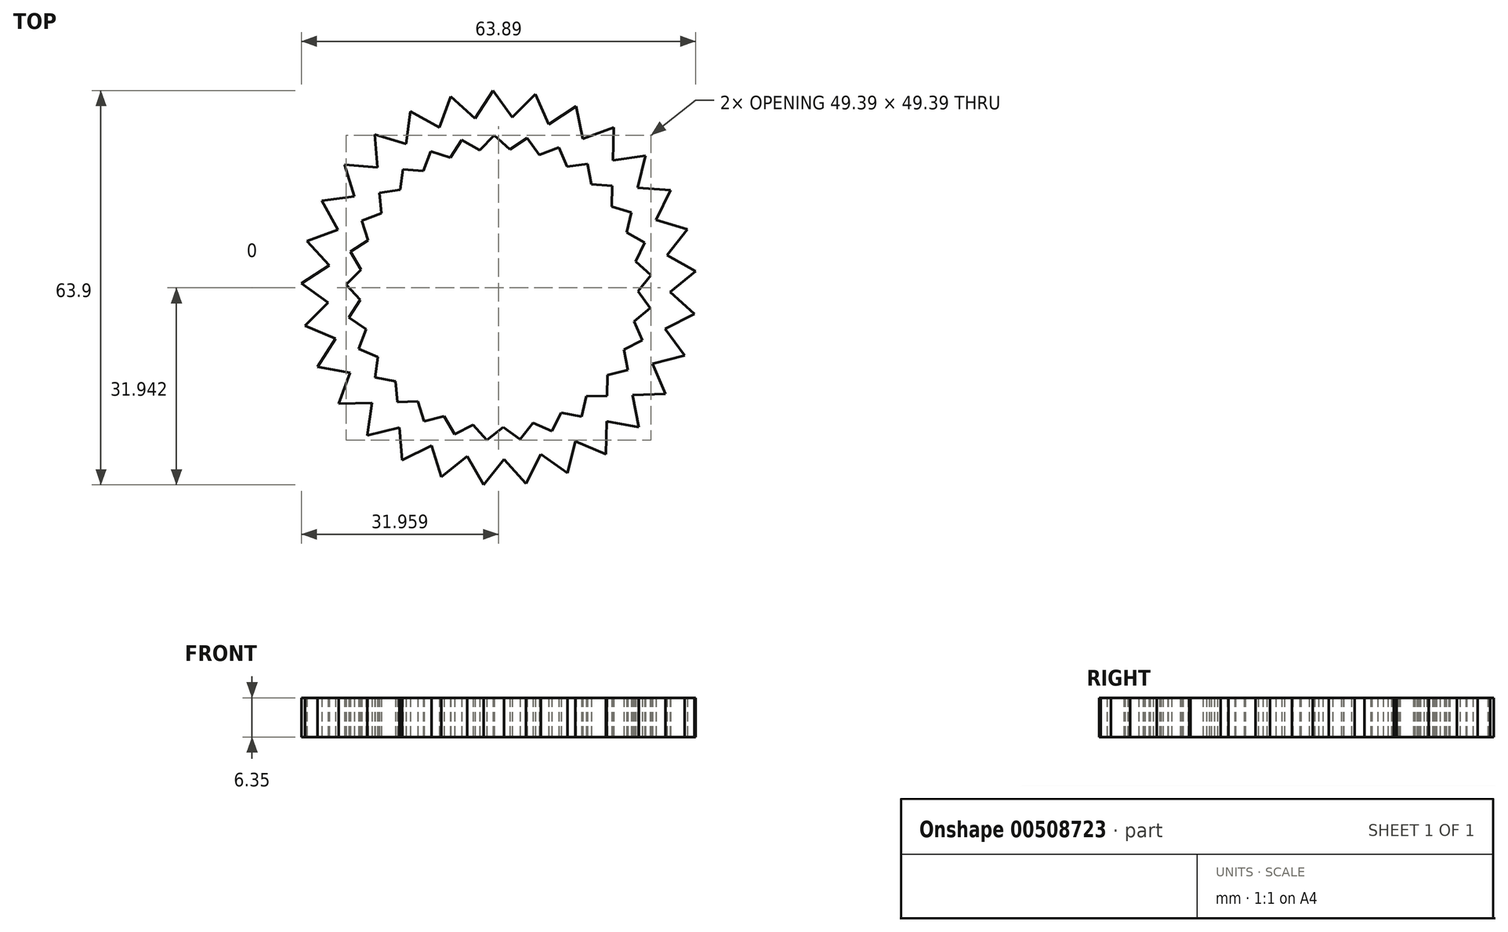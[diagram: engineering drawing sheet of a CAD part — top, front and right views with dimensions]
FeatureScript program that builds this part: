
annotation { "Feature Type Name" : "Feature", "Feature Type Description" : "" }
export const myFeature = defineFeature(function(context is Context, id is Id, definition is map)
    precondition{}
    {
        {
            var Q0;
            Q0=qCreatedBy(makeId("Top.planeOp"),FACE);
            var sketch = newSketch(context, id + "F0", { "sketchPlane" : qUnion([Q0])});
            skLineSegment(sketch, "E0", {"start": v(-25.94, -18.75) * mm, "end": v(-7.82, 31.04) * mm});
            skLineSegment(sketch, "E1", {"start": v(-7.82, 31.04) * mm, "end": v(31.73, -4.22) * mm});
            skLineSegment(sketch, "E2", {"start": v(31.73, -4.22) * mm, "end": v(-15.66, -27.91) * mm});
            skLineSegment(sketch, "E3", {"start": v(-15.66, -27.91) * mm, "end": v(-20.13, 24.88) * mm});
            skLineSegment(sketch, "E4", {"start": v(-20.13, 24.88) * mm, "end": v(30.57, 9.5) * mm});
            skLineSegment(sketch, "E5", {"start": v(30.57, 9.5) * mm, "end": v(-2.5, -31.9) * mm});
            skLineSegment(sketch, "E6", {"start": v(-2.5, -31.9) * mm, "end": v(-28.72, 14.13) * mm});
            skLineSegment(sketch, "E7", {"start": v(-28.72, 14.13) * mm, "end": v(23.76, 21.45) * mm});
            skLineSegment(sketch, "E8", {"start": v(23.76, 21.45) * mm, "end": v(11.13, -30) * mm});
            skLineSegment(sketch, "E9", {"start": v(11.13, -30) * mm, "end": v(-32, 0.77) * mm});
            skLineSegment(sketch, "E10", {"start": v(-32, 0.77) * mm, "end": v(12.55, 29.44) * mm});
            skLineSegment(sketch, "E11", {"start": v(12.55, 29.44) * mm, "end": v(22.7, -22.56) * mm});
            skLineSegment(sketch, "E12", {"start": v(22.7, -22.56) * mm, "end": v(-29.36, -12.74) * mm});
            skLineSegment(sketch, "E13", {"start": v(-29.36, -12.74) * mm, "end": v(-0.97, 32) * mm});
            skLineSegment(sketch, "E14", {"start": v(-0.97, 32) * mm, "end": v(30.08, -10.94) * mm});
            skLineSegment(sketch, "E15", {"start": v(30.08, -10.94) * mm, "end": v(-21.3, -23.9) * mm});
            skLineSegment(sketch, "E16", {"start": v(-21.3, -23.9) * mm, "end": v(-14.31, 28.63) * mm});
            skLineSegment(sketch, "E17", {"start": v(-14.31, 28.63) * mm, "end": v(31.9, 2.7) * mm});
            skLineSegment(sketch, "E18", {"start": v(31.9, 2.7) * mm, "end": v(-9.3, -30.63) * mm});
            skLineSegment(sketch, "E19", {"start": v(-9.3, -30.63) * mm, "end": v(-25, 19.97) * mm});
            skLineSegment(sketch, "E20", {"start": v(-25, 19.97) * mm, "end": v(27.81, 15.84) * mm});
            skLineSegment(sketch, "E21", {"start": v(27.81, 15.84) * mm, "end": v(4.42, -31.7) * mm});
            skLineSegment(sketch, "E22", {"start": v(4.42, -31.7) * mm, "end": v(-31.08, 7.63) * mm});
            skLineSegment(sketch, "E23", {"start": v(-31.08, 7.63) * mm, "end": v(18.6, 26.05) * mm});
            skLineSegment(sketch, "E24", {"start": v(18.6, 26.05) * mm, "end": v(17.32, -26.91) * mm});
            skLineSegment(sketch, "E25", {"start": v(17.32, -26.91) * mm, "end": v(-31.41, -6.13) * mm});
            skLineSegment(sketch, "E26", {"start": v(-31.41, -6.13) * mm, "end": v(5.93, 31.45) * mm});
            skLineSegment(sketch, "E27", {"start": v(5.93, 31.45) * mm, "end": v(27.02, -17.15) * mm});
            skLineSegment(sketch, "E28", {"start": v(27.02, -17.15) * mm, "end": v(-25.94, -18.75) * mm});
            skSolve(sketch);
        }
        {
            var Q0;
            {var subQ0=sQuery(id+"F0.wireOp",EDGE,"E28");var subQ1=sQuery(id+"F0.wireOp",EDGE,"E0");var subQ2=makeQuery(id+"F0.imprint","INTERSECT",VERTEX,{"derivedFrom":[subQ1,subQ0]});Q0=makeQuery(id+"F0.imprint","IMPRINT",FACE,{"disambiguationData":[TD([[makeQuery(id+"F0.imprint","IMPRINT",EDGE,{"disambiguationData":[TD([[subQ2,-1.0]])],"derivedFrom":subQ1}),-1.0]])]});}
            var Q1;
            {var subQ0=sQuery(id+"F0.wireOp",EDGE,"E15");var subQ1=sQuery(id+"F0.wireOp",EDGE,"E3");var subQ2=makeQuery(id+"F0.imprint","INTERSECT",VERTEX,{"derivedFrom":[subQ1,subQ0]});Q1=makeQuery(id+"F0.imprint","IMPRINT",FACE,{"disambiguationData":[TD([[makeQuery(id+"F0.imprint","IMPRINT",EDGE,{"disambiguationData":[TD([[subQ2,-1.0]])],"derivedFrom":subQ1}),1.0]])]});}
            var Q2;
            {var subQ0=sQuery(id+"F0.wireOp",EDGE,"E3");var subQ1=sQuery(id+"F0.wireOp",EDGE,"E2");var subQ2=makeQuery(id+"F0.imprint","INTERSECT",VERTEX,{"derivedFrom":[subQ1,subQ0]});Q2=makeQuery(id+"F0.imprint","IMPRINT",FACE,{"disambiguationData":[TD([[makeQuery(id+"F0.imprint","IMPRINT",EDGE,{"disambiguationData":[TD([[subQ2,1.0]])],"derivedFrom":subQ1}),-1.0]])]});}
            var Q3;
            {var subQ0=sQuery(id+"F0.wireOp",EDGE,"E19");var subQ1=sQuery(id+"F0.wireOp",EDGE,"E2");var subQ2=makeQuery(id+"F0.imprint","INTERSECT",VERTEX,{"derivedFrom":[subQ1,subQ0]});Q3=makeQuery(id+"F0.imprint","IMPRINT",FACE,{"disambiguationData":[TD([[makeQuery(id+"F0.imprint","IMPRINT",EDGE,{"disambiguationData":[TD([[subQ2,1.0]])],"derivedFrom":subQ1}),1.0]])]});}
            var Q4;
            {var subQ0=sQuery(id+"F0.wireOp",EDGE,"E6");var subQ1=sQuery(id+"F0.wireOp",EDGE,"E5");var subQ2=makeQuery(id+"F0.imprint","INTERSECT",VERTEX,{"derivedFrom":[subQ1,subQ0]});Q4=makeQuery(id+"F0.imprint","IMPRINT",FACE,{"disambiguationData":[TD([[makeQuery(id+"F0.imprint","IMPRINT",EDGE,{"disambiguationData":[TD([[subQ2,1.0]])],"derivedFrom":subQ1}),-1.0]])]});}
            var Q5;
            {var subQ0=sQuery(id+"F0.wireOp",EDGE,"E9");var subQ1=sQuery(id+"F0.wireOp",EDGE,"E8");var subQ2=makeQuery(id+"F0.imprint","INTERSECT",VERTEX,{"derivedFrom":[subQ1,subQ0]});Q5=makeQuery(id+"F0.imprint","IMPRINT",FACE,{"disambiguationData":[TD([[makeQuery(id+"F0.imprint","IMPRINT",EDGE,{"disambiguationData":[TD([[subQ2,1.0]])],"derivedFrom":subQ1}),-1.0]])]});}
            var Q6;
            {var subQ0=sQuery(id+"F0.wireOp",EDGE,"E25");var subQ1=sQuery(id+"F0.wireOp",EDGE,"E8");var subQ2=makeQuery(id+"F0.imprint","INTERSECT",VERTEX,{"derivedFrom":[subQ1,subQ0]});Q6=makeQuery(id+"F0.imprint","IMPRINT",FACE,{"disambiguationData":[TD([[makeQuery(id+"F0.imprint","IMPRINT",EDGE,{"disambiguationData":[TD([[subQ2,1.0]])],"derivedFrom":subQ1}),1.0]])]});}
            var Q7;
            {var subQ0=sQuery(id+"F0.wireOp",EDGE,"E12");var subQ1=sQuery(id+"F0.wireOp",EDGE,"E11");var subQ2=makeQuery(id+"F0.imprint","INTERSECT",VERTEX,{"derivedFrom":[subQ1,subQ0]});Q7=makeQuery(id+"F0.imprint","IMPRINT",FACE,{"disambiguationData":[TD([[makeQuery(id+"F0.imprint","IMPRINT",EDGE,{"disambiguationData":[TD([[subQ2,1.0]])],"derivedFrom":subQ1}),-1.0]])]});}
            var Q8;
            {var subQ0=sQuery(id+"F0.wireOp",EDGE,"E28");var subQ1=sQuery(id+"F0.wireOp",EDGE,"E11");var subQ2=makeQuery(id+"F0.imprint","INTERSECT",VERTEX,{"derivedFrom":[subQ1,subQ0]});Q8=makeQuery(id+"F0.imprint","IMPRINT",FACE,{"disambiguationData":[TD([[makeQuery(id+"F0.imprint","IMPRINT",EDGE,{"disambiguationData":[TD([[subQ2,1.0]])],"derivedFrom":subQ1}),1.0]])]});}
            var Q9;
            {var subQ0=sQuery(id+"F0.wireOp",EDGE,"E14");var subQ1=sQuery(id+"F0.wireOp",EDGE,"E2");var subQ2=makeQuery(id+"F0.imprint","INTERSECT",VERTEX,{"derivedFrom":[subQ1,subQ0]});Q9=makeQuery(id+"F0.imprint","IMPRINT",FACE,{"disambiguationData":[TD([[makeQuery(id+"F0.imprint","IMPRINT",EDGE,{"disambiguationData":[TD([[subQ2,-1.0]])],"derivedFrom":subQ1}),1.0]])]});}
            var Q10;
            {var subQ0=sQuery(id+"F0.wireOp",EDGE,"E2");var subQ1=sQuery(id+"F0.wireOp",EDGE,"E1");var subQ2=makeQuery(id+"F0.imprint","INTERSECT",VERTEX,{"derivedFrom":[subQ1,subQ0]});Q10=makeQuery(id+"F0.imprint","IMPRINT",FACE,{"disambiguationData":[TD([[makeQuery(id+"F0.imprint","IMPRINT",EDGE,{"disambiguationData":[TD([[subQ2,1.0]])],"derivedFrom":subQ1}),-1.0]])]});}
            var Q11;
            {var subQ0=sQuery(id+"F0.wireOp",EDGE,"E18");var subQ1=sQuery(id+"F0.wireOp",EDGE,"E1");var subQ2=makeQuery(id+"F0.imprint","INTERSECT",VERTEX,{"derivedFrom":[subQ1,subQ0]});Q11=makeQuery(id+"F0.imprint","IMPRINT",FACE,{"disambiguationData":[TD([[makeQuery(id+"F0.imprint","IMPRINT",EDGE,{"disambiguationData":[TD([[subQ2,1.0]])],"derivedFrom":subQ1}),1.0]])]});}
            var Q12;
            {var subQ0=sQuery(id+"F0.wireOp",EDGE,"E5");var subQ1=sQuery(id+"F0.wireOp",EDGE,"E4");var subQ2=makeQuery(id+"F0.imprint","INTERSECT",VERTEX,{"derivedFrom":[subQ1,subQ0]});Q12=makeQuery(id+"F0.imprint","IMPRINT",FACE,{"disambiguationData":[TD([[makeQuery(id+"F0.imprint","IMPRINT",EDGE,{"disambiguationData":[TD([[subQ2,1.0]])],"derivedFrom":subQ1}),-1.0]])]});}
            var Q13;
            {var subQ0=sQuery(id+"F0.wireOp",EDGE,"E21");var subQ1=sQuery(id+"F0.wireOp",EDGE,"E4");var subQ2=makeQuery(id+"F0.imprint","INTERSECT",VERTEX,{"derivedFrom":[subQ1,subQ0]});Q13=makeQuery(id+"F0.imprint","IMPRINT",FACE,{"disambiguationData":[TD([[makeQuery(id+"F0.imprint","IMPRINT",EDGE,{"disambiguationData":[TD([[subQ2,1.0]])],"derivedFrom":subQ1}),1.0]])]});}
            var Q14;
            {var subQ0=sQuery(id+"F0.wireOp",EDGE,"E8");var subQ1=sQuery(id+"F0.wireOp",EDGE,"E7");var subQ2=makeQuery(id+"F0.imprint","INTERSECT",VERTEX,{"derivedFrom":[subQ1,subQ0]});Q14=makeQuery(id+"F0.imprint","IMPRINT",FACE,{"disambiguationData":[TD([[makeQuery(id+"F0.imprint","IMPRINT",EDGE,{"disambiguationData":[TD([[subQ2,1.0]])],"derivedFrom":subQ1}),-1.0]])]});}
            var Q15;
            {var subQ0=sQuery(id+"F0.wireOp",EDGE,"E24");var subQ1=sQuery(id+"F0.wireOp",EDGE,"E7");var subQ2=makeQuery(id+"F0.imprint","INTERSECT",VERTEX,{"derivedFrom":[subQ1,subQ0]});Q15=makeQuery(id+"F0.imprint","IMPRINT",FACE,{"disambiguationData":[TD([[makeQuery(id+"F0.imprint","IMPRINT",EDGE,{"disambiguationData":[TD([[subQ2,1.0]])],"derivedFrom":subQ1}),1.0]])]});}
            var Q16;
            {var subQ0=sQuery(id+"F0.wireOp",EDGE,"E11");var subQ1=sQuery(id+"F0.wireOp",EDGE,"E10");var subQ2=makeQuery(id+"F0.imprint","INTERSECT",VERTEX,{"derivedFrom":[subQ1,subQ0]});Q16=makeQuery(id+"F0.imprint","IMPRINT",FACE,{"disambiguationData":[TD([[makeQuery(id+"F0.imprint","IMPRINT",EDGE,{"disambiguationData":[TD([[subQ2,1.0]])],"derivedFrom":subQ1}),-1.0]])]});}
            var Q17;
            {var subQ0=sQuery(id+"F0.wireOp",EDGE,"E27");var subQ1=sQuery(id+"F0.wireOp",EDGE,"E10");var subQ2=makeQuery(id+"F0.imprint","INTERSECT",VERTEX,{"derivedFrom":[subQ1,subQ0]});Q17=makeQuery(id+"F0.imprint","IMPRINT",FACE,{"disambiguationData":[TD([[makeQuery(id+"F0.imprint","IMPRINT",EDGE,{"disambiguationData":[TD([[subQ2,1.0]])],"derivedFrom":subQ1}),1.0]])]});}
            var Q18;
            {var subQ0=sQuery(id+"F0.wireOp",EDGE,"E13");var subQ1=sQuery(id+"F0.wireOp",EDGE,"E1");var subQ2=makeQuery(id+"F0.imprint","INTERSECT",VERTEX,{"derivedFrom":[subQ1,subQ0]});Q18=makeQuery(id+"F0.imprint","IMPRINT",FACE,{"disambiguationData":[TD([[makeQuery(id+"F0.imprint","IMPRINT",EDGE,{"disambiguationData":[TD([[subQ2,-1.0]])],"derivedFrom":subQ1}),1.0]])]});}
            var Q19;
            {var subQ0=sQuery(id+"F0.wireOp",EDGE,"E1");var subQ1=sQuery(id+"F0.wireOp",EDGE,"E0");var subQ2=makeQuery(id+"F0.imprint","INTERSECT",VERTEX,{"derivedFrom":[subQ1,subQ0]});Q19=makeQuery(id+"F0.imprint","IMPRINT",FACE,{"disambiguationData":[TD([[makeQuery(id+"F0.imprint","IMPRINT",EDGE,{"disambiguationData":[TD([[subQ2,1.0]])],"derivedFrom":subQ1}),-1.0]])]});}
            var Q20;
            {var subQ0=sQuery(id+"F0.wireOp",EDGE,"E17");var subQ1=sQuery(id+"F0.wireOp",EDGE,"E0");var subQ2=makeQuery(id+"F0.imprint","INTERSECT",VERTEX,{"derivedFrom":[subQ1,subQ0]});Q20=makeQuery(id+"F0.imprint","IMPRINT",FACE,{"disambiguationData":[TD([[makeQuery(id+"F0.imprint","IMPRINT",EDGE,{"disambiguationData":[TD([[subQ2,1.0]])],"derivedFrom":subQ1}),1.0]])]});}
            var Q21;
            {var subQ0=sQuery(id+"F0.wireOp",EDGE,"E4");var subQ1=sQuery(id+"F0.wireOp",EDGE,"E3");var subQ2=makeQuery(id+"F0.imprint","INTERSECT",VERTEX,{"derivedFrom":[subQ1,subQ0]});Q21=makeQuery(id+"F0.imprint","IMPRINT",FACE,{"disambiguationData":[TD([[makeQuery(id+"F0.imprint","IMPRINT",EDGE,{"disambiguationData":[TD([[subQ2,1.0]])],"derivedFrom":subQ1}),-1.0]])]});}
            var Q22;
            {var subQ0=sQuery(id+"F0.wireOp",EDGE,"E20");var subQ1=sQuery(id+"F0.wireOp",EDGE,"E3");var subQ2=makeQuery(id+"F0.imprint","INTERSECT",VERTEX,{"derivedFrom":[subQ1,subQ0]});Q22=makeQuery(id+"F0.imprint","IMPRINT",FACE,{"disambiguationData":[TD([[makeQuery(id+"F0.imprint","IMPRINT",EDGE,{"disambiguationData":[TD([[subQ2,1.0]])],"derivedFrom":subQ1}),1.0]])]});}
            var Q23;
            {var subQ0=sQuery(id+"F0.wireOp",EDGE,"E7");var subQ1=sQuery(id+"F0.wireOp",EDGE,"E6");var subQ2=makeQuery(id+"F0.imprint","INTERSECT",VERTEX,{"derivedFrom":[subQ1,subQ0]});Q23=makeQuery(id+"F0.imprint","IMPRINT",FACE,{"disambiguationData":[TD([[makeQuery(id+"F0.imprint","IMPRINT",EDGE,{"disambiguationData":[TD([[subQ2,1.0]])],"derivedFrom":subQ1}),-1.0]])]});}
            var Q24;
            {var subQ0=sQuery(id+"F0.wireOp",EDGE,"E23");var subQ1=sQuery(id+"F0.wireOp",EDGE,"E6");var subQ2=makeQuery(id+"F0.imprint","INTERSECT",VERTEX,{"derivedFrom":[subQ1,subQ0]});Q24=makeQuery(id+"F0.imprint","IMPRINT",FACE,{"disambiguationData":[TD([[makeQuery(id+"F0.imprint","IMPRINT",EDGE,{"disambiguationData":[TD([[subQ2,1.0]])],"derivedFrom":subQ1}),1.0]])]});}
            var Q25;
            {var subQ0=sQuery(id+"F0.wireOp",EDGE,"E10");var subQ1=sQuery(id+"F0.wireOp",EDGE,"E9");var subQ2=makeQuery(id+"F0.imprint","INTERSECT",VERTEX,{"derivedFrom":[subQ1,subQ0]});Q25=makeQuery(id+"F0.imprint","IMPRINT",FACE,{"disambiguationData":[TD([[makeQuery(id+"F0.imprint","IMPRINT",EDGE,{"disambiguationData":[TD([[subQ2,1.0]])],"derivedFrom":subQ1}),-1.0]])]});}
            var Q26;
            {var subQ0=sQuery(id+"F0.wireOp",EDGE,"E26");var subQ1=sQuery(id+"F0.wireOp",EDGE,"E9");var subQ2=makeQuery(id+"F0.imprint","INTERSECT",VERTEX,{"derivedFrom":[subQ1,subQ0]});Q26=makeQuery(id+"F0.imprint","IMPRINT",FACE,{"disambiguationData":[TD([[makeQuery(id+"F0.imprint","IMPRINT",EDGE,{"disambiguationData":[TD([[subQ2,1.0]])],"derivedFrom":subQ1}),1.0]])]});}
            var Q27;
            {var subQ0=sQuery(id+"F0.wireOp",EDGE,"E12");var subQ1=sQuery(id+"F0.wireOp",EDGE,"E0");var subQ2=makeQuery(id+"F0.imprint","INTERSECT",VERTEX,{"derivedFrom":[subQ1,subQ0]});Q27=makeQuery(id+"F0.imprint","IMPRINT",FACE,{"disambiguationData":[TD([[makeQuery(id+"F0.imprint","IMPRINT",EDGE,{"disambiguationData":[TD([[subQ2,-1.0]])],"derivedFrom":subQ1}),1.0]])]});}
            var Q28;
            {var subQ0=sQuery(id+"F0.wireOp",EDGE,"E22");var subQ1=sQuery(id+"F0.wireOp",EDGE,"E5");var subQ2=makeQuery(id+"F0.imprint","INTERSECT",VERTEX,{"derivedFrom":[subQ1,subQ0]});Q28=makeQuery(id+"F0.imprint","IMPRINT",FACE,{"disambiguationData":[TD([[makeQuery(id+"F0.imprint","IMPRINT",EDGE,{"disambiguationData":[TD([[subQ2,1.0]])],"derivedFrom":subQ1}),1.0]])]});}
            var Q29;
            {var subQ0=sQuery(id+"F0.wireOp",EDGE,"E19");var subQ1=sQuery(id+"F0.wireOp",EDGE,"E2");var subQ2=makeQuery(id+"F0.imprint","INTERSECT",VERTEX,{"derivedFrom":[subQ1,subQ0]});Q29=makeQuery(id+"F0.imprint","IMPRINT",FACE,{"disambiguationData":[TD([[makeQuery(id+"F0.imprint","IMPRINT",EDGE,{"disambiguationData":[TD([[subQ2,1.0]])],"derivedFrom":subQ1}),-1.0]])]});}
            var Q30;
            {var subQ0=sQuery(id+"F0.wireOp",EDGE,"E22");var subQ1=sQuery(id+"F0.wireOp",EDGE,"E5");var subQ2=makeQuery(id+"F0.imprint","INTERSECT",VERTEX,{"derivedFrom":[subQ1,subQ0]});Q30=makeQuery(id+"F0.imprint","IMPRINT",FACE,{"disambiguationData":[TD([[makeQuery(id+"F0.imprint","IMPRINT",EDGE,{"disambiguationData":[TD([[subQ2,1.0]])],"derivedFrom":subQ1}),-1.0]])]});}
            var Q31;
            {var subQ0=sQuery(id+"F0.wireOp",EDGE,"E22");var subQ1=sQuery(id+"F0.wireOp",EDGE,"E2");var subQ2=makeQuery(id+"F0.imprint","INTERSECT",VERTEX,{"derivedFrom":[subQ1,subQ0]});Q31=makeQuery(id+"F0.imprint","IMPRINT",FACE,{"disambiguationData":[TD([[makeQuery(id+"F0.imprint","IMPRINT",EDGE,{"disambiguationData":[TD([[subQ2,-1.0]])],"derivedFrom":subQ1}),1.0]])]});}
            var Q32;
            {var subQ0=sQuery(id+"F0.wireOp",EDGE,"E25");var subQ1=sQuery(id+"F0.wireOp",EDGE,"E5");var subQ2=makeQuery(id+"F0.imprint","INTERSECT",VERTEX,{"derivedFrom":[subQ1,subQ0]});Q32=makeQuery(id+"F0.imprint","IMPRINT",FACE,{"disambiguationData":[TD([[makeQuery(id+"F0.imprint","IMPRINT",EDGE,{"disambiguationData":[TD([[subQ2,-1.0]])],"derivedFrom":subQ1}),1.0]])]});}
            var Q33;
            {var subQ0=sQuery(id+"F0.wireOp",EDGE,"E25");var subQ1=sQuery(id+"F0.wireOp",EDGE,"E8");var subQ2=makeQuery(id+"F0.imprint","INTERSECT",VERTEX,{"derivedFrom":[subQ1,subQ0]});Q33=makeQuery(id+"F0.imprint","IMPRINT",FACE,{"disambiguationData":[TD([[makeQuery(id+"F0.imprint","IMPRINT",EDGE,{"disambiguationData":[TD([[subQ2,1.0]])],"derivedFrom":subQ1}),-1.0]])]});}
            var Q34;
            {var subQ0=sQuery(id+"F0.wireOp",EDGE,"E28");var subQ1=sQuery(id+"F0.wireOp",EDGE,"E11");var subQ2=makeQuery(id+"F0.imprint","INTERSECT",VERTEX,{"derivedFrom":[subQ1,subQ0]});Q34=makeQuery(id+"F0.imprint","IMPRINT",FACE,{"disambiguationData":[TD([[makeQuery(id+"F0.imprint","IMPRINT",EDGE,{"disambiguationData":[TD([[subQ2,1.0]])],"derivedFrom":subQ1}),-1.0]])]});}
            var Q35;
            {var subQ0=sQuery(id+"F0.wireOp",EDGE,"E26");var subQ1=sQuery(id+"F0.wireOp",EDGE,"E9");var subQ2=makeQuery(id+"F0.imprint","INTERSECT",VERTEX,{"derivedFrom":[subQ1,subQ0]});Q35=makeQuery(id+"F0.imprint","IMPRINT",FACE,{"disambiguationData":[TD([[makeQuery(id+"F0.imprint","IMPRINT",EDGE,{"disambiguationData":[TD([[subQ2,1.0]])],"derivedFrom":subQ1}),-1.0]])]});}
            var Q36;
            {var subQ0=sQuery(id+"F0.wireOp",EDGE,"E25");var subQ1=sQuery(id+"F0.wireOp",EDGE,"E0");var subQ2=makeQuery(id+"F0.imprint","INTERSECT",VERTEX,{"derivedFrom":[subQ1,subQ0]});Q36=makeQuery(id+"F0.imprint","IMPRINT",FACE,{"disambiguationData":[TD([[makeQuery(id+"F0.imprint","IMPRINT",EDGE,{"disambiguationData":[TD([[subQ2,-1.0]])],"derivedFrom":subQ1}),1.0]])]});}
            var Q37;
            {var subQ0=sQuery(id+"F0.wireOp",EDGE,"E12");var subQ1=sQuery(id+"F0.wireOp",EDGE,"E0");var subQ2=makeQuery(id+"F0.imprint","INTERSECT",VERTEX,{"derivedFrom":[subQ1,subQ0]});Q37=makeQuery(id+"F0.imprint","IMPRINT",FACE,{"disambiguationData":[TD([[makeQuery(id+"F0.imprint","IMPRINT",EDGE,{"disambiguationData":[TD([[subQ2,-1.0]])],"derivedFrom":subQ1}),-1.0]])]});}
            var Q38;
            {var subQ0=sQuery(id+"F0.wireOp",EDGE,"E28");var subQ1=sQuery(id+"F0.wireOp",EDGE,"E3");var subQ2=makeQuery(id+"F0.imprint","INTERSECT",VERTEX,{"derivedFrom":[subQ1,subQ0]});Q38=makeQuery(id+"F0.imprint","IMPRINT",FACE,{"disambiguationData":[TD([[makeQuery(id+"F0.imprint","IMPRINT",EDGE,{"disambiguationData":[TD([[subQ2,-1.0]])],"derivedFrom":subQ1}),1.0]])]});}
            var Q39;
            {var subQ0=sQuery(id+"F0.wireOp",EDGE,"E15");var subQ1=sQuery(id+"F0.wireOp",EDGE,"E3");var subQ2=makeQuery(id+"F0.imprint","INTERSECT",VERTEX,{"derivedFrom":[subQ1,subQ0]});Q39=makeQuery(id+"F0.imprint","IMPRINT",FACE,{"disambiguationData":[TD([[makeQuery(id+"F0.imprint","IMPRINT",EDGE,{"disambiguationData":[TD([[subQ2,-1.0]])],"derivedFrom":subQ1}),-1.0]])]});}
            var Q40;
            {var subQ0=sQuery(id+"F0.wireOp",EDGE,"E28");var subQ1=sQuery(id+"F0.wireOp",EDGE,"E8");var subQ2=makeQuery(id+"F0.imprint","INTERSECT",VERTEX,{"derivedFrom":[subQ1,subQ0]});Q40=makeQuery(id+"F0.imprint","IMPRINT",FACE,{"disambiguationData":[TD([[makeQuery(id+"F0.imprint","IMPRINT",EDGE,{"disambiguationData":[TD([[subQ2,-1.0]])],"derivedFrom":subQ1}),1.0]])]});}
            var Q41;
            {var subQ0=sQuery(id+"F0.wireOp",EDGE,"E27");var subQ1=sQuery(id+"F0.wireOp",EDGE,"E2");var subQ2=makeQuery(id+"F0.imprint","INTERSECT",VERTEX,{"derivedFrom":[subQ1,subQ0]});Q41=makeQuery(id+"F0.imprint","IMPRINT",FACE,{"disambiguationData":[TD([[makeQuery(id+"F0.imprint","IMPRINT",EDGE,{"disambiguationData":[TD([[subQ2,-1.0]])],"derivedFrom":subQ1}),1.0]])]});}
            var Q42;
            {var subQ0=sQuery(id+"F0.wireOp",EDGE,"E14");var subQ1=sQuery(id+"F0.wireOp",EDGE,"E2");var subQ2=makeQuery(id+"F0.imprint","INTERSECT",VERTEX,{"derivedFrom":[subQ1,subQ0]});Q42=makeQuery(id+"F0.imprint","IMPRINT",FACE,{"disambiguationData":[TD([[makeQuery(id+"F0.imprint","IMPRINT",EDGE,{"disambiguationData":[TD([[subQ2,-1.0]])],"derivedFrom":subQ1}),-1.0]])]});}
            var Q43;
            {var subQ0=sQuery(id+"F0.wireOp",EDGE,"E18");var subQ1=sQuery(id+"F0.wireOp",EDGE,"E1");var subQ2=makeQuery(id+"F0.imprint","INTERSECT",VERTEX,{"derivedFrom":[subQ1,subQ0]});Q43=makeQuery(id+"F0.imprint","IMPRINT",FACE,{"disambiguationData":[TD([[makeQuery(id+"F0.imprint","IMPRINT",EDGE,{"disambiguationData":[TD([[subQ2,1.0]])],"derivedFrom":subQ1}),-1.0]])]});}
            var Q44;
            {var subQ0=sQuery(id+"F0.wireOp",EDGE,"E21");var subQ1=sQuery(id+"F0.wireOp",EDGE,"E1");var subQ2=makeQuery(id+"F0.imprint","INTERSECT",VERTEX,{"derivedFrom":[subQ1,subQ0]});Q44=makeQuery(id+"F0.imprint","IMPRINT",FACE,{"disambiguationData":[TD([[makeQuery(id+"F0.imprint","IMPRINT",EDGE,{"disambiguationData":[TD([[subQ2,-1.0]])],"derivedFrom":subQ1}),1.0]])]});}
            var Q45;
            {var subQ0=sQuery(id+"F0.wireOp",EDGE,"E21");var subQ1=sQuery(id+"F0.wireOp",EDGE,"E4");var subQ2=makeQuery(id+"F0.imprint","INTERSECT",VERTEX,{"derivedFrom":[subQ1,subQ0]});Q45=makeQuery(id+"F0.imprint","IMPRINT",FACE,{"disambiguationData":[TD([[makeQuery(id+"F0.imprint","IMPRINT",EDGE,{"disambiguationData":[TD([[subQ2,1.0]])],"derivedFrom":subQ1}),-1.0]])]});}
            var Q46;
            {var subQ0=sQuery(id+"F0.wireOp",EDGE,"E24");var subQ1=sQuery(id+"F0.wireOp",EDGE,"E4");var subQ2=makeQuery(id+"F0.imprint","INTERSECT",VERTEX,{"derivedFrom":[subQ1,subQ0]});Q46=makeQuery(id+"F0.imprint","IMPRINT",FACE,{"disambiguationData":[TD([[makeQuery(id+"F0.imprint","IMPRINT",EDGE,{"disambiguationData":[TD([[subQ2,-1.0]])],"derivedFrom":subQ1}),1.0]])]});}
            var Q47;
            {var subQ0=sQuery(id+"F0.wireOp",EDGE,"E24");var subQ1=sQuery(id+"F0.wireOp",EDGE,"E7");var subQ2=makeQuery(id+"F0.imprint","INTERSECT",VERTEX,{"derivedFrom":[subQ1,subQ0]});Q47=makeQuery(id+"F0.imprint","IMPRINT",FACE,{"disambiguationData":[TD([[makeQuery(id+"F0.imprint","IMPRINT",EDGE,{"disambiguationData":[TD([[subQ2,1.0]])],"derivedFrom":subQ1}),-1.0]])]});}
            var Q48;
            {var subQ0=sQuery(id+"F0.wireOp",EDGE,"E27");var subQ1=sQuery(id+"F0.wireOp",EDGE,"E7");var subQ2=makeQuery(id+"F0.imprint","INTERSECT",VERTEX,{"derivedFrom":[subQ1,subQ0]});Q48=makeQuery(id+"F0.imprint","IMPRINT",FACE,{"disambiguationData":[TD([[makeQuery(id+"F0.imprint","IMPRINT",EDGE,{"disambiguationData":[TD([[subQ2,-1.0]])],"derivedFrom":subQ1}),1.0]])]});}
            var Q49;
            {var subQ0=sQuery(id+"F0.wireOp",EDGE,"E27");var subQ1=sQuery(id+"F0.wireOp",EDGE,"E10");var subQ2=makeQuery(id+"F0.imprint","INTERSECT",VERTEX,{"derivedFrom":[subQ1,subQ0]});Q49=makeQuery(id+"F0.imprint","IMPRINT",FACE,{"disambiguationData":[TD([[makeQuery(id+"F0.imprint","IMPRINT",EDGE,{"disambiguationData":[TD([[subQ2,1.0]])],"derivedFrom":subQ1}),-1.0]])]});}
            var Q50;
            {var subQ0=sQuery(id+"F0.wireOp",EDGE,"E26");var subQ1=sQuery(id+"F0.wireOp",EDGE,"E1");var subQ2=makeQuery(id+"F0.imprint","INTERSECT",VERTEX,{"derivedFrom":[subQ1,subQ0]});Q50=makeQuery(id+"F0.imprint","IMPRINT",FACE,{"disambiguationData":[TD([[makeQuery(id+"F0.imprint","IMPRINT",EDGE,{"disambiguationData":[TD([[subQ2,-1.0]])],"derivedFrom":subQ1}),1.0]])]});}
            var Q51;
            {var subQ0=sQuery(id+"F0.wireOp",EDGE,"E13");var subQ1=sQuery(id+"F0.wireOp",EDGE,"E1");var subQ2=makeQuery(id+"F0.imprint","INTERSECT",VERTEX,{"derivedFrom":[subQ1,subQ0]});Q51=makeQuery(id+"F0.imprint","IMPRINT",FACE,{"disambiguationData":[TD([[makeQuery(id+"F0.imprint","IMPRINT",EDGE,{"disambiguationData":[TD([[subQ2,-1.0]])],"derivedFrom":subQ1}),-1.0]])]});}
            var Q52;
            {var subQ0=sQuery(id+"F0.wireOp",EDGE,"E17");var subQ1=sQuery(id+"F0.wireOp",EDGE,"E0");var subQ2=makeQuery(id+"F0.imprint","INTERSECT",VERTEX,{"derivedFrom":[subQ1,subQ0]});Q52=makeQuery(id+"F0.imprint","IMPRINT",FACE,{"disambiguationData":[TD([[makeQuery(id+"F0.imprint","IMPRINT",EDGE,{"disambiguationData":[TD([[subQ2,1.0]])],"derivedFrom":subQ1}),-1.0]])]});}
            var Q53;
            {var subQ0=sQuery(id+"F0.wireOp",EDGE,"E20");var subQ1=sQuery(id+"F0.wireOp",EDGE,"E0");var subQ2=makeQuery(id+"F0.imprint","INTERSECT",VERTEX,{"derivedFrom":[subQ1,subQ0]});Q53=makeQuery(id+"F0.imprint","IMPRINT",FACE,{"disambiguationData":[TD([[makeQuery(id+"F0.imprint","IMPRINT",EDGE,{"disambiguationData":[TD([[subQ2,-1.0]])],"derivedFrom":subQ1}),1.0]])]});}
            var Q54;
            {var subQ0=sQuery(id+"F0.wireOp",EDGE,"E20");var subQ1=sQuery(id+"F0.wireOp",EDGE,"E3");var subQ2=makeQuery(id+"F0.imprint","INTERSECT",VERTEX,{"derivedFrom":[subQ1,subQ0]});Q54=makeQuery(id+"F0.imprint","IMPRINT",FACE,{"disambiguationData":[TD([[makeQuery(id+"F0.imprint","IMPRINT",EDGE,{"disambiguationData":[TD([[subQ2,1.0]])],"derivedFrom":subQ1}),-1.0]])]});}
            var Q55;
            {var subQ0=sQuery(id+"F0.wireOp",EDGE,"E23");var subQ1=sQuery(id+"F0.wireOp",EDGE,"E3");var subQ2=makeQuery(id+"F0.imprint","INTERSECT",VERTEX,{"derivedFrom":[subQ1,subQ0]});Q55=makeQuery(id+"F0.imprint","IMPRINT",FACE,{"disambiguationData":[TD([[makeQuery(id+"F0.imprint","IMPRINT",EDGE,{"disambiguationData":[TD([[subQ2,-1.0]])],"derivedFrom":subQ1}),1.0]])]});}
            var Q56;
            {var subQ0=sQuery(id+"F0.wireOp",EDGE,"E23");var subQ1=sQuery(id+"F0.wireOp",EDGE,"E6");var subQ2=makeQuery(id+"F0.imprint","INTERSECT",VERTEX,{"derivedFrom":[subQ1,subQ0]});Q56=makeQuery(id+"F0.imprint","IMPRINT",FACE,{"disambiguationData":[TD([[makeQuery(id+"F0.imprint","IMPRINT",EDGE,{"disambiguationData":[TD([[subQ2,1.0]])],"derivedFrom":subQ1}),-1.0]])]});}
            var Q57;
            {var subQ0=sQuery(id+"F0.wireOp",EDGE,"E26");var subQ1=sQuery(id+"F0.wireOp",EDGE,"E6");var subQ2=makeQuery(id+"F0.imprint","INTERSECT",VERTEX,{"derivedFrom":[subQ1,subQ0]});Q57=makeQuery(id+"F0.imprint","IMPRINT",FACE,{"disambiguationData":[TD([[makeQuery(id+"F0.imprint","IMPRINT",EDGE,{"disambiguationData":[TD([[subQ2,-1.0]])],"derivedFrom":subQ1}),1.0]])]});}
            extrude(context, id + "F1", {"entities" : qUnion([Q0, Q1, Q2, Q3, Q4, Q5, Q6, Q7, Q8, Q9, Q10, Q11, Q12, Q13, Q14, Q15, Q16, Q17, Q18, Q19, Q20, Q21, Q22, Q23, Q24, Q25, Q26, Q27, Q28, Q29, Q30, Q31, Q32, Q33, Q34, Q35, Q36, Q37, Q38, Q39, Q40, Q41, Q42, Q43, Q44, Q45, Q46, Q47, Q48, Q49, Q50, Q51, Q52, Q53, Q54, Q55, Q56, Q57]), "depth" : 6.35 * mm, "offsetDistance" : 25.4 * mm});
        }
    });
